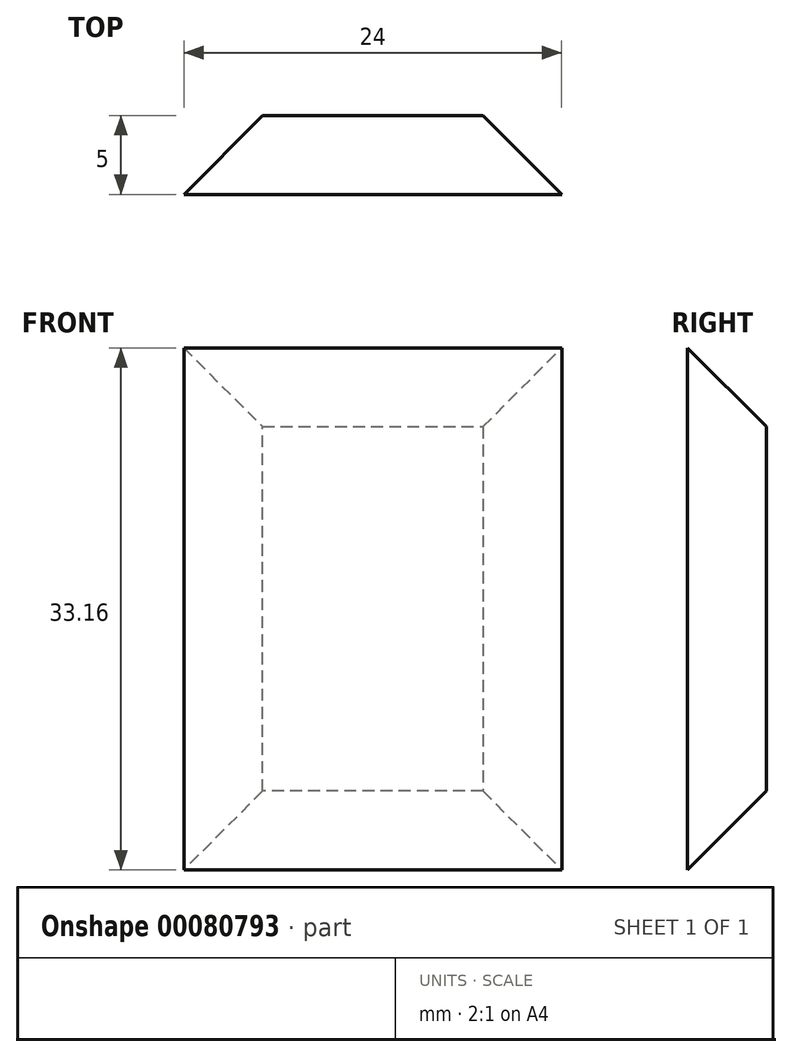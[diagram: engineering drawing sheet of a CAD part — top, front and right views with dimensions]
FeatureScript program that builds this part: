
annotation { "Feature Type Name" : "Feature", "Feature Type Description" : "" }
export const myFeature = defineFeature(function(context is Context, id is Id, definition is map)
    precondition{}
    {
        {
            var Q0;
            Q0=qCreatedBy(makeId("Front.planeOp"),FACE);
            var sketch = newSketch(context, id + "F0", { "sketchPlane" : qUnion([Q0])});
            skLineSegment(sketch, "E0.bottom", {"start": v(-12, 16.58) * mm, "end": v(12, 16.58) * mm});
            skLineSegment(sketch, "E0.top", {"start": v(-12, -16.58) * mm, "end": v(12, -16.58) * mm});
            skLineSegment(sketch, "E0.left", {"start": v(-12, 16.58) * mm, "end": v(-12, -16.58) * mm});
            skLineSegment(sketch, "E0.right", {"start": v(12, 16.58) * mm, "end": v(12, -16.58) * mm});
            skPoint(sketch, "E0.middle", {"position": v(0, 0) * mm});
            skSolve(sketch);
        }
        {
            var Q0;
            Q0=makeQuery(id+"F0.imprint","IMPRINT",FACE,{"disambiguationData":[TD([[makeQuery(id+"F0.imprint","IMPRINT",EDGE,{"derivedFrom":sQuery(id+"F0.wireOp",EDGE,"E0.bottom")}),-1.0]])]});
            extrude(context, id + "F1", {"entities" : qUnion([Q0]), "depth" : 5 * mm});
        }
        {
            var Q0;
            Q0=makeQuery(id+"F1.opExtrude","CAP_EDGE",EDGE,{"disambiguationData":[OSD([sQuery(id+"F0.wireOp",EDGE,"E0.left")])],"isStart":true});
            var Q1;
            Q1=makeQuery(id+"F1.opExtrude","CAP_FACE",FACE,{"disambiguationData":[OSD([sQuery(id+"F0.wireOp",EDGE,"E0.bottom"),sQuery(id+"F0.wireOp",EDGE,"E0.top"),sQuery(id+"F0.wireOp",EDGE,"E0.left"),sQuery(id+"F0.wireOp",EDGE,"E0.right")])],"isStart":true});
            chamfer(context, id + "F2", {"entities" : qUnion([Q0, Q1]), "width" : 5 * mm, "tangentPropagation" : true});
        }
    });
